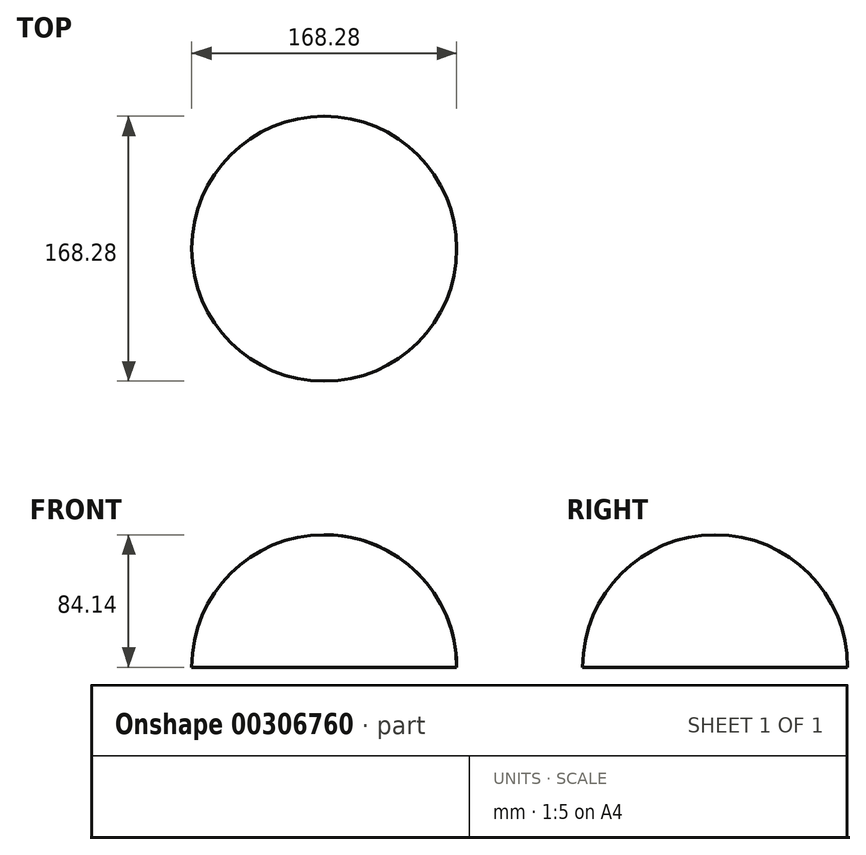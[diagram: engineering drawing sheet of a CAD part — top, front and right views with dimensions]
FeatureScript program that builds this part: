
annotation { "Feature Type Name" : "Feature", "Feature Type Description" : "" }
export const myFeature = defineFeature(function(context is Context, id is Id, definition is map)
    precondition{}
    {
        {
            var Q0;
            Q0=qCreatedBy(makeId("Front.planeOp"),FACE);
            var sketch = newSketch(context, id + "F0", { "sketchPlane" : qUnion([Q0])});
            skArc(sketch, "E0", {"start": v(84.14, 0) * mm, "mid": v(59.5, 59.5) * mm, "end": v(0, 84.14) * mm});
            skLineSegment(sketch, "E1", {"start": v(0, 0) * mm, "end": v(84.14, 0) * mm});
            skLineSegment(sketch, "E2", {"start": v(0, 84.14) * mm, "end": v(0, 0) * mm});
            skPoint(sketch, "E3.end.orphan", {"position": v(-84.14, 0) * mm});
            skSolve(sketch);
        }
        {
            var Q0;
            Q0 = qSketchRegion(id + "F0", true);
            var Q1;
            Q1=sQuery(id+"F0.wireOp",EDGE,"E2");
            revolve(context, id + "F1", {"entities" : qUnion([Q0]), "axis" : qUnion([Q1]), "revolveType" : RevolveType.FULL});
        }
        {
            var Q0;
            Q0=qCreatedBy(makeId("Front.planeOp"),FACE);
            cPlane(context, id + "F2", {"entities" : qUnion([Q0]), "cplaneType" : CPlaneType.OFFSET, "offset" : 101.6 * mm, "width" : 152.4 * mm, "height" : 152.4 * mm});
        }
    });
